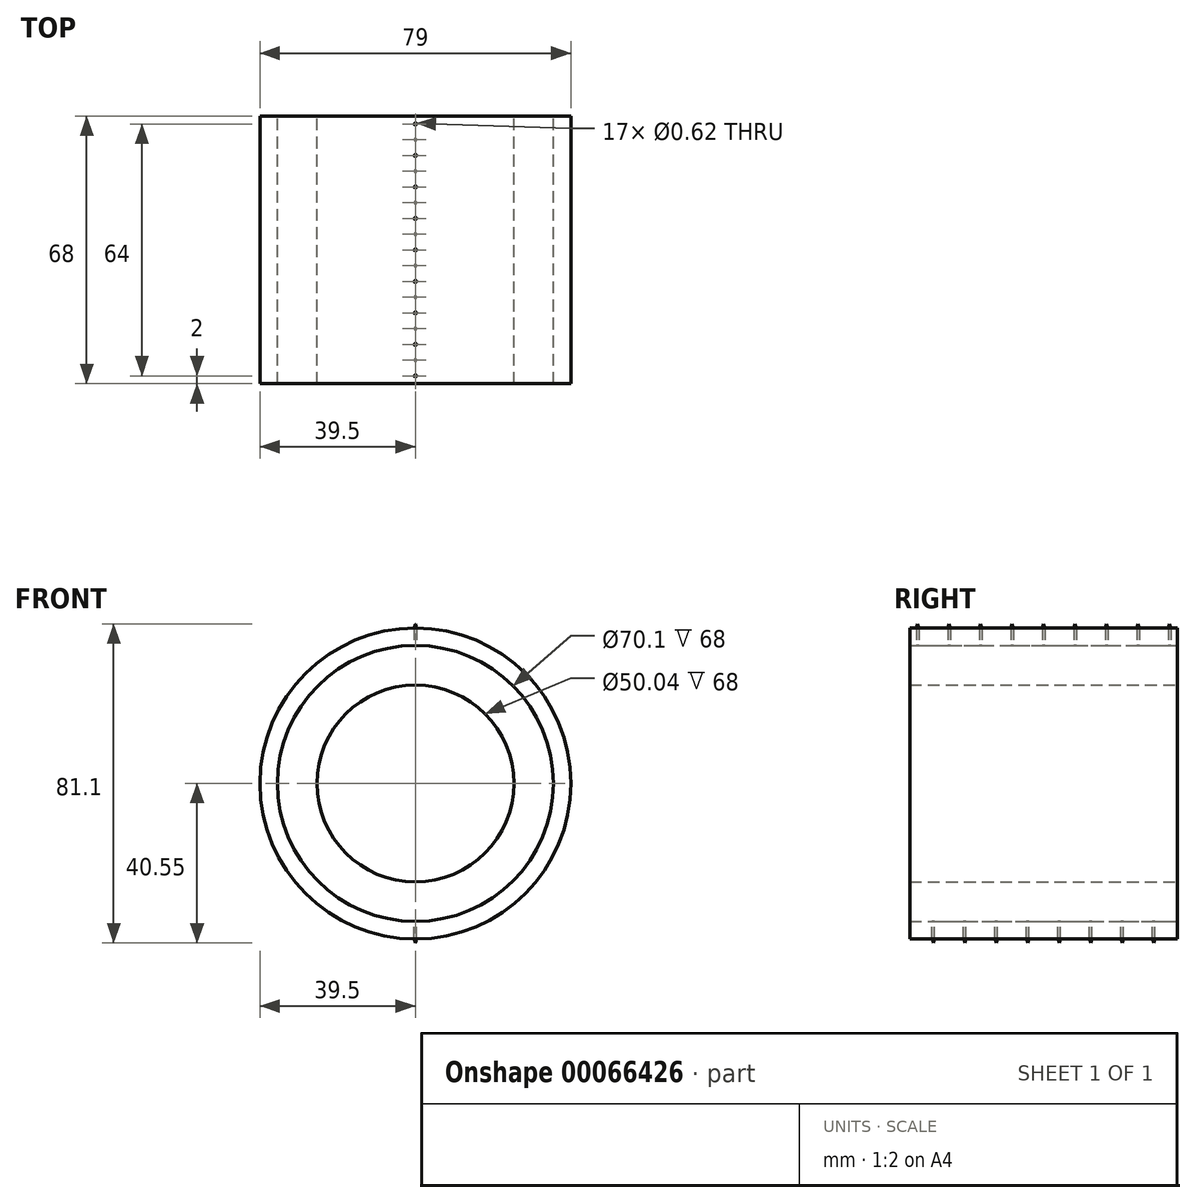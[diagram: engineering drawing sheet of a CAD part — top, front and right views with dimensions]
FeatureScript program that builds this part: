
annotation { "Feature Type Name" : "Feature", "Feature Type Description" : "" }
export const myFeature = defineFeature(function(context is Context, id is Id, definition is map)
    precondition{}
    {
        {
            var Q0;
            Q0=qCreatedBy(makeId("Front.planeOp"),FACE);
            var sketch = newSketch(context, id + "F0", { "sketchPlane" : qUnion([Q0])});
            skCircle(sketch, "E0", {"center": v(0, 0) * mm, "radius": 25.02 * mm});
            skCircle(sketch, "E1", {"center": v(0, 0) * mm, "radius": 35.05 * mm});
            skSolve(sketch);
        }
        {
            var Q0;
            Q0=makeQuery(id+"F0.imprint","IMPRINT",FACE,{"disambiguationData":[TD([[makeQuery(id+"F0.imprint","IMPRINT",EDGE,{"derivedFrom":sQuery(id+"F0.wireOp",EDGE,"E0")}),-1.0]])]});
            extrude(context, id + "F1", {"entities" : qUnion([Q0]), "endBound" : BoundingType.SYMMETRIC, "depth" : 68 * mm});
        }
        {
            var Q0;
            Q0=qCreatedBy(makeId("Front.planeOp"),FACE);
            var sketch = newSketch(context, id + "F2", { "sketchPlane" : qUnion([Q0])});
            skCircle(sketch, "E2.0", {"center": v(0, 0) * mm, "radius": 35.05 * mm});
            skCircle(sketch, "E3", {"center": v(0, 0) * mm, "radius": 39.5 * mm});
            skSolve(sketch);
        }
        {
            var Q0;
            Q0=makeQuery(id+"F2.imprint","IMPRINT",FACE,{"disambiguationData":[TD([[makeQuery(id+"F2.imprint","IMPRINT",EDGE,{"derivedFrom":sQuery(id+"F2.wireOp",EDGE,"E2.0")}),-1.0]])]});
            extrude(context, id + "F3", {"entities" : qUnion([Q0]), "endBound" : BoundingType.SYMMETRIC, "depth" : 68 * mm});
        }
        {
            var Q0;
            Q0=qCreatedBy(makeId("Top.planeOp"),FACE);
            cPlane(context, id + "F4", {"entities" : qUnion([Q0]), "cplaneType" : CPlaneType.OFFSET, "offset" : 70.1 / 2 * mm, "width" : 152.4 * mm, "height" : 152.4 * mm});
        }
        {
            var Q0;
            Q0=qCreatedBy(id+"F4.planeOp",FACE);
            var sketch = newSketch(context, id + "F5", { "sketchPlane" : qUnion([Q0])});
            skCircle(sketch, "E4", {"center": v(0, 0) * mm, "radius": 0.31 * mm});
            skCircle(sketch, "E5.0.1.0", {"center": v(0, 8) * mm, "radius": 0.31 * mm});
            skCircle(sketch, "E5.0.2.0", {"center": v(0, 16) * mm, "radius": 0.31 * mm});
            skCircle(sketch, "E5.0.3.0", {"center": v(0, 24) * mm, "radius": 0.31 * mm});
            skCircle(sketch, "E5.0.4.0", {"center": v(0, 32) * mm, "radius": 0.31 * mm});
            skLineSegment(sketch, "E5.direction1", {"start": v(0, 0) * mm, "end": v(25.4, 0) * mm, "construction": true});
            skLineSegment(sketch, "E5.direction2", {"start": v(0, 0) * mm, "end": v(0, 8) * mm, "construction": true});
            skCircle(sketch, "E6.0.1.0", {"center": v(0, -8) * mm, "radius": 0.31 * mm});
            skCircle(sketch, "E6.0.2.0", {"center": v(0, -16) * mm, "radius": 0.31 * mm});
            skCircle(sketch, "E6.0.3.0", {"center": v(0, -24) * mm, "radius": 0.31 * mm});
            skCircle(sketch, "E6.0.4.0", {"center": v(0, -32) * mm, "radius": 0.31 * mm});
            skLineSegment(sketch, "E6.direction2", {"start": v(0, 0) * mm, "end": v(0, -8) * mm, "construction": true});
            skSolve(sketch);
        }
        {
            var Q0;
            Q0=qSketchRegion(id+"F5",true);
            extrude(context, id + "F6", {"entities" : qUnion([Q0]), "operationType" : NewBodyOperationType.REMOVE, "depth" : 25.4 * mm});
        }
        {
            var Q0;
            Q0=qSketchRegion(id+"F5",true);
            extrude(context, id + "F7", {"entities" : qUnion([Q0]), "depth" : 5.5 * mm});
        }
        {
            var Q0;
            Q0=makeQuery(id+"F7.opExtrude","CAP_EDGE",EDGE,{"disambiguationData":[OSD([sQuery(id+"F5.wireOp",EDGE,"E6.0.4.0")])],"isStart":false});
            var Q1;
            Q1=makeQuery(id+"F7.opExtrude","CAP_EDGE",EDGE,{"disambiguationData":[OSD([sQuery(id+"F5.wireOp",EDGE,"E6.0.3.0")])],"isStart":false});
            var Q2;
            Q2=makeQuery(id+"F7.opExtrude","CAP_EDGE",EDGE,{"disambiguationData":[OSD([sQuery(id+"F5.wireOp",EDGE,"E6.0.2.0")])],"isStart":false});
            var Q3;
            Q3=makeQuery(id+"F7.opExtrude","CAP_EDGE",EDGE,{"disambiguationData":[OSD([sQuery(id+"F5.wireOp",EDGE,"E6.0.1.0")])],"isStart":false});
            var Q4;
            Q4=makeQuery(id+"F7.opExtrude","CAP_EDGE",EDGE,{"disambiguationData":[OSD([sQuery(id+"F5.wireOp",EDGE,"E4")])],"isStart":false});
            var Q5;
            Q5=makeQuery(id+"F7.opExtrude","CAP_EDGE",EDGE,{"disambiguationData":[OSD([sQuery(id+"F5.wireOp",EDGE,"E5.0.1.0")])],"isStart":false});
            var Q6;
            Q6=makeQuery(id+"F7.opExtrude","CAP_EDGE",EDGE,{"disambiguationData":[OSD([sQuery(id+"F5.wireOp",EDGE,"E5.0.2.0")])],"isStart":false});
            var Q7;
            Q7=makeQuery(id+"F7.opExtrude","CAP_EDGE",EDGE,{"disambiguationData":[OSD([sQuery(id+"F5.wireOp",EDGE,"E5.0.3.0")])],"isStart":false});
            var Q8;
            Q8=makeQuery(id+"F7.opExtrude","CAP_EDGE",EDGE,{"disambiguationData":[OSD([sQuery(id+"F5.wireOp",EDGE,"E5.0.4.0")])],"isStart":false});
            chamfer(context, id + "F8", {"entities" : qUnion([Q0, Q1, Q2, Q3, Q4, Q5, Q6, Q7, Q8]), "chamferType" : ChamferType.TWO_OFFSETS, "width1" : 0.31 * mm, "oppositeDirection" : false, "width2" : 1.1 * mm});
        }
        {
            var Q0;
            Q0=qCreatedBy(makeId("Top.planeOp"),FACE);
            cPlane(context, id + "F9", {"entities" : qUnion([Q0]), "cplaneType" : CPlaneType.OFFSET, "offset" : 70.1 * mm / 2, "oppositeDirection" : true, "width" : 152.4 * mm, "height" : 152.4 * mm});
        }
        {
            var Q0;
            Q0=qCreatedBy(id+"F9.planeOp",FACE);
            var sketch = newSketch(context, id + "F10", { "sketchPlane" : qUnion([Q0])});
            skCircle(sketch, "E7", {"center": v(0, -4) * mm, "radius": 0.31 * mm});
            skCircle(sketch, "E8", {"center": v(0, 4) * mm, "radius": 0.31 * mm});
            skCircle(sketch, "E9.0.1.0", {"center": v(0, -12) * mm, "radius": 0.31 * mm});
            skCircle(sketch, "E9.0.2.0", {"center": v(0, -20) * mm, "radius": 0.31 * mm});
            skCircle(sketch, "E9.0.3.0", {"center": v(0, -28) * mm, "radius": 0.31 * mm});
            skLineSegment(sketch, "E9.direction1", {"start": v(0, -4) * mm, "end": v(20.95, -4) * mm, "construction": true});
            skLineSegment(sketch, "E9.direction2", {"start": v(0, -4) * mm, "end": v(0, -12) * mm, "construction": true});
            skCircle(sketch, "E10.0.1.0", {"center": v(0, 12) * mm, "radius": 0.31 * mm});
            skCircle(sketch, "E10.0.2.0", {"center": v(0, 20) * mm, "radius": 0.31 * mm});
            skCircle(sketch, "E10.0.3.0", {"center": v(0, 28) * mm, "radius": 0.31 * mm});
            skLineSegment(sketch, "E10.direction1", {"start": v(0, 4) * mm, "end": v(25.4, 4) * mm, "construction": true});
            skLineSegment(sketch, "E10.direction2", {"start": v(0, 4) * mm, "end": v(0, 12) * mm, "construction": true});
            skSolve(sketch);
        }
        {
            var Q0;
            Q0=qSketchRegion(id+"F10",true);
            extrude(context, id + "F11", {"entities" : qUnion([Q0]), "operationType" : NewBodyOperationType.REMOVE, "oppositeDirection" : true, "depth" : 25.4 * mm});
        }
        {
            var Q0;
            Q0=qSketchRegion(id+"F10",true);
            extrude(context, id + "F12", {"entities" : qUnion([Q0]), "oppositeDirection" : true, "depth" : 5.5 * mm});
        }
        {
            var Q0;
            Q0=makeQuery(id+"F12.opExtrude","CAP_EDGE",EDGE,{"disambiguationData":[OSD([sQuery(id+"F10.wireOp",EDGE,"E9.0.3.0")])],"isStart":false});
            var Q1;
            Q1=makeQuery(id+"F12.opExtrude","CAP_EDGE",EDGE,{"disambiguationData":[OSD([sQuery(id+"F10.wireOp",EDGE,"E9.0.2.0")])],"isStart":false});
            var Q2;
            Q2=makeQuery(id+"F12.opExtrude","CAP_EDGE",EDGE,{"disambiguationData":[OSD([sQuery(id+"F10.wireOp",EDGE,"E9.0.1.0")])],"isStart":false});
            var Q3;
            Q3=makeQuery(id+"F12.opExtrude","CAP_EDGE",EDGE,{"disambiguationData":[OSD([sQuery(id+"F10.wireOp",EDGE,"E7")])],"isStart":false});
            var Q4;
            Q4=makeQuery(id+"F12.opExtrude","CAP_EDGE",EDGE,{"disambiguationData":[OSD([sQuery(id+"F10.wireOp",EDGE,"E8")])],"isStart":false});
            var Q5;
            Q5=makeQuery(id+"F12.opExtrude","CAP_EDGE",EDGE,{"disambiguationData":[OSD([sQuery(id+"F10.wireOp",EDGE,"E10.0.1.0")])],"isStart":false});
            var Q6;
            Q6=makeQuery(id+"F12.opExtrude","CAP_EDGE",EDGE,{"disambiguationData":[OSD([sQuery(id+"F10.wireOp",EDGE,"E10.0.2.0")])],"isStart":false});
            var Q7;
            Q7=makeQuery(id+"F12.opExtrude","CAP_EDGE",EDGE,{"disambiguationData":[OSD([sQuery(id+"F10.wireOp",EDGE,"E10.0.3.0")])],"isStart":false});
            chamfer(context, id + "F13", {"entities" : qUnion([Q0, Q1, Q2, Q3, Q4, Q5, Q6, Q7]), "chamferType" : ChamferType.TWO_OFFSETS, "width1" : 1.1 * mm, "oppositeDirection" : false, "width2" : 0.31 * mm, "tangentPropagation" : true});
        }
    });
